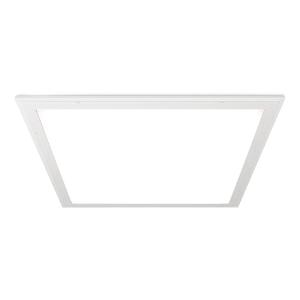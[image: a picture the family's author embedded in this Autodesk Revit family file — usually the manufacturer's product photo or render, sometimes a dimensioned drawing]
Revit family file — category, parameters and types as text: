
# Revit family: 3f_filippi_-_l_650_luce_diffusa_vss_3f_filippi_-_21897_-_l_650_75w-940_dali_vss_599x599
name_source: partatom
category: Lighting Fixtures
units: mm (PartAtom-declared; Revit-internal decimal feet)

## family parameters
Cut with Voids When Loaded = No
Host = Face
Light Source = No
Part Type = Normal
Room Calculation Point = No
Round Connector Dimension = Use Diameter
Shared = No

## types (1)
- 3F Filippi - L 650 Luce Diffusa VSS (1 x LED, 6830 lm, 81 W, 4000 K)
    Apparent Load = 81 VA
    Approval mark = ENEC
    CIE Flux Codes = 63 92 98 100 100
    Color Rendering = 90
    Color Temperature = 4000 K
    Control Gear = Electronic transformer
    Default Elevation = 1800 mm
    Description = ILLUMINOTECHNICAL
Luminous efficiency 100% (DLOR 100%, ULOR 0%).
Initial luminous flux of the luminaire 6830 lm.
Direct symmetric distribution.
Installation Interdistance Transv.D = 1.17 x hu - Long.D = 1.16 x hu.
Average luminance <3000 cd/m² for radial angles >65°.
Tabular UGR (CIE 117 - 4H-8H; S=0.25H; 70/50/20): RUG 19.1 - 18.9.
Beam angle: 90° - 88°.
Luminous efficacy 84 lm/W.
Lifetime (L93/B10): 30000 h. (tq+25°C)
Lifetime (L90/B10): 50000 h. (tq+25°C)
Lifetime (L85/B10): 80000 h. (tq+25°C)
Lifetime (L80/B10): 100000 h. (tq+25°C)
Sudden decreased luminous flux after 50000 hours: 0% (C0).
Photobiological safety in compliance with IEC/TR 62778: RG0 risk exempt, (IEC 62471).
In compliance with IEC/EN 62722-2-1 - IEC/EN 62717 standards.

SOURCE
Squared LED module 75W/940.
Source with special protection against aggressive chemically-volatile substances for standard LED technology.
Energy efficiency class (UE 2019/2020 - UE 2019/2015): E.
CIE 13.3 Colour rendering index: CRI >90 (R9 >50%).
IES TM-30 Fidelity Index: Rf = 92 Rg = 101.
CCT nominal colour temperature 4000 K.
Colour initial tolerance (MacAdam): SDCM 3.

MECHANICAL
Housing in galvannealed steel, painted in white epoxy-polyester.
Perimetral frame in white stainless steel.
VSS moulded laminated dipped glass, non-combustible, thickness 7 mm.
Anti-glare opal polycarbonate filter for brightness uniformity.
The version 599x599 is dedicated to modular metal false ceilings with dimensions of 600x600.
Luminaire with limited surface temperature. - D - (EN 60598-2-24)
Dimensions: 599x599 mm, height 90 mm. Weight 10.675 kg.
IP66 protection degree for exposed part, IP64 for recessed part.
Mechanical strength to impacts IK08 (5 joule).
Glow-wire test resistance 650°C.

ELECTRICAL
Halogen Free DALI-2 DATI (Parts 251, 252, 253), PUSH-DIM, electronic wiring 230V-50/60Hz, power factor 0.95 at full load, THD <25%, constant output current, SELV, class I, 1 driver, 1 DALI addresse.
Power of the luminaire 81 W.
CE - IEC 60598-1 - EN 60598-1.
SAFE FLICKER: PstLM=<1 and SVM=<0.4 (IEC TR 61547-1 and IEC TR 63158), to ensure a more comfortable and safe light.
Luminaire compliant with EN 60598-2-22 for power supply from a centralised emergency system CPSS (Central Power Supply System), not incorporated in the luminaire - high risk areas excluded. The default power and flux are 100% in AC and 15% in DC.
Ambient temperature from 0°C to +40°C.
Temperature class T6 max 85°C.
5-pole terminal block (L-N-PE-DA/DA) quick connection for line connection with connection capacity 2x2.5 mm² per poles.
Relative humidity UR: <85%.

INSTALLATION
Trimless recessed fitting, to be used with inspectable false-ceilings that can be inspected using fixing brackets which are always required, also designed for the hanging from rough ceiling.
All accessories dedicated to this product are available on the Catalog and on our website www.3F-Filippi.com.

APPLICATIONS
Suitable product for food production plants (HACCP), IFS (Food Version 6), BRC (GSFS Food Version 7).
Environments: hospital premises, transit areas, laboratories, platform-roof, underpasses.
Environments: sterilized, aseptic.
In hospital environments, food industry or machines with parts in motion, with considerable sudden temperature changes, and in general in any environments requiring total protection against falling fragments, use luminaires with laminated glass only.
Tempered glass is not immune to falling fragments from harmless and caused by shocks or exceptionally derived from the tempering process.
Environments requiring a high level of protection and simplified cleaning.
Environments with exacting visual tasks, where diffused soft light for optimum visual comfort is required.

LIGHT MANAGEMENT
Recommended minimum setting: 10%.
The luminaire, equipped with (DALI-2 DATI) driver, can be controlled manually with 3F Easy Dim technology or automatically/manually with wired or wireless DALI/D2D control systems.
The D2D driver guarantees interoperability with other devices with the same certification by making the following information available:
Device Data (Part 251), Energy Report (Part 252), Diagnosis & Maintenance (Part 253).
In electrical systems without a regulation system (manual or automatic) and DALI bus, a suitable jumper must be made on the DA-DA terminals of the appliance.

WARNING
Luminaire designed for disposal/recycling at end-of-life.
Replaceable (LED only) light source by a professional. Replaceable control gear by a professional.
    Height = 0 mm  [stored 0 ft]
    Lamp = 1 x LED
    Lamp Light Flux = 6830 lm
    Lamp Power = 81 W
    Lamp count = 1
    Length = 599 mm
    Lifetime = 50000 h
    Luminous efficacy = 84 lm/W
    Manufacturer = 3F Filippi
    ModVariant = No
    Model = 3F Filippi - 21897 - L 650 75W-940 DALI VSS 599x599
    Mounting Place = Ceiling
    Mounting Type = Recessed
    Number of Poles = 1
    OnlyDefault = Yes
    Power Factor = 1
    Product Name = 3F Filippi - L 650 Luce Diffusa VSS
    Product group = recessed luminaire
    ProductGroupID = 4
    Protection Class = Protection class I
    Protection Degree = IP 64
    RLX_Detail_Level = 1
    RLX_Emergency_Light_Flux = 0 lm
    RLX_Emergency_Type = 0
    RLX_Emergency_Type_DB = No
    RlxData = <blob elided: 101073 chars, md5=440a6d55>
    Socket = socket
    Standby Power = 0 W
    System Light Flux = 6830 lm
    System Power = 81 W
    Type Comments = Product without accessories
    Type Image = 3ffilippi_l_650_luce_diffusa_vss.jpg
    URL = http://relux.com
    VarID = ---
    Voltage = 0 V
    Weight = 0.00 kg
    Width = 599 mm

note: [stored X ft] marks values corroborated as IEEE doubles in the binary element streams (Revit-internal decimal feet)

## geometry (parser evidence)
native form markers: Blend x4, Sweep x11
no freeform markers — native parametric forms only
